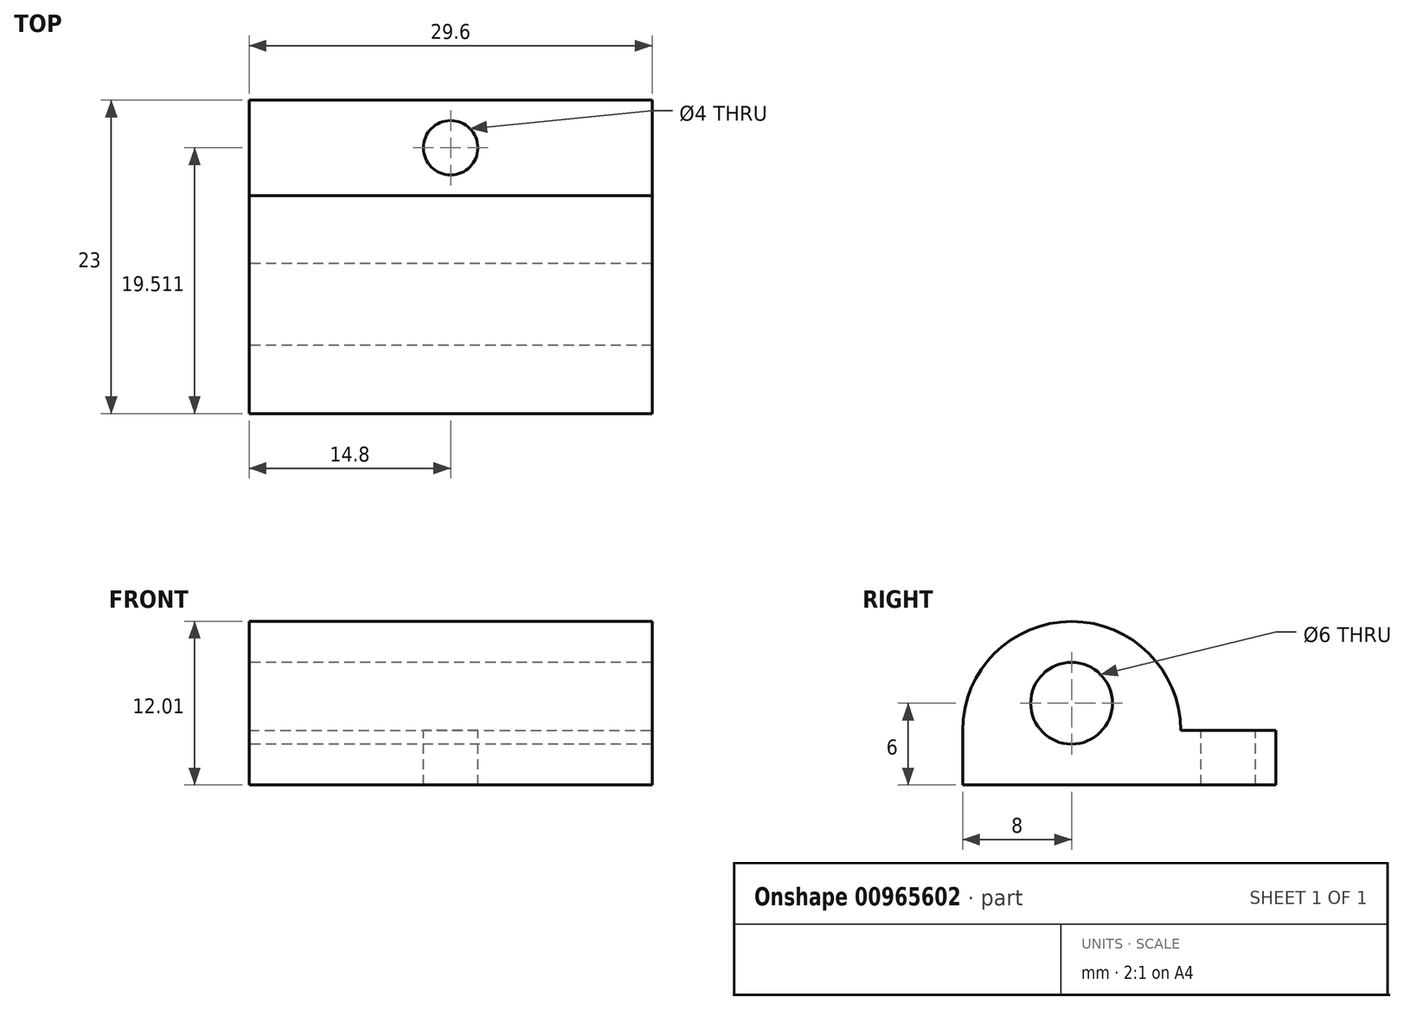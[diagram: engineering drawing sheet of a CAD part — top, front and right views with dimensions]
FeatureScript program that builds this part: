
annotation { "Feature Type Name" : "Feature", "Feature Type Description" : "" }
export const myFeature = defineFeature(function(context is Context, id is Id, definition is map)
    precondition{}
    {
        {
            var Q0;
            Q0=qCreatedBy(makeId("Top.planeOp"),FACE);
            var sketch = newSketch(context, id + "F0", { "sketchPlane" : qUnion([Q0])});
            skLineSegment(sketch, "E0.bottom", {"start": v(-14.8, 5) * mm, "end": v(14.8, 5) * mm});
            skLineSegment(sketch, "E0.top", {"start": v(-14.8, -5) * mm, "end": v(14.8, -5) * mm});
            skLineSegment(sketch, "E0.left", {"start": v(-14.8, 5) * mm, "end": v(-14.8, -5) * mm});
            skLineSegment(sketch, "E0.right", {"start": v(14.8, 5) * mm, "end": v(14.8, -5) * mm});
            skLineSegment(sketch, "E1.bottom", {"start": v(-14.8, 10) * mm, "end": v(14.8, 10) * mm});
            skLineSegment(sketch, "E1.top", {"start": v(-14.8, -10) * mm, "end": v(14.8, -10) * mm});
            skLineSegment(sketch, "E1.left", {"start": v(-14.8, 10) * mm, "end": v(-14.8, -10) * mm});
            skLineSegment(sketch, "E1.right", {"start": v(14.8, 10) * mm, "end": v(14.8, -10) * mm});
            skSolve(sketch);
        }
        {
            var Q0;
            {var subQ5=sQuery(id+"F0.wireOp",EDGE,"E1.bottom");Q0=makeQuery(id+"F0.imprint","IMPRINT",FACE,{"disambiguationData":[TD([[makeQuery(id+"F0.imprint","IMPRINT",EDGE,{"derivedFrom":subQ5}),-1.0]])]});}
            var Q1;
            {var subQ0=sQuery(id+"F0.wireOp",EDGE,"E1.left");var subQ1=sQuery(id+"F0.wireOp",EDGE,"E0.bottom");var subQ2=makeQuery(id+"F0.imprint","INTERSECT",VERTEX,{"derivedFrom":[subQ1,subQ0]});Q1=makeQuery(id+"F0.imprint","IMPRINT",FACE,{"disambiguationData":[TD([[makeQuery(id+"F0.imprint","IMPRINT",EDGE,{"disambiguationData":[TD([[subQ2,-1.0]])],"derivedFrom":subQ1}),-1.0]])]});}
            var Q2;
            {var subQ5=sQuery(id+"F0.wireOp",EDGE,"E1.top");Q2=makeQuery(id+"F0.imprint","IMPRINT",FACE,{"disambiguationData":[TD([[makeQuery(id+"F0.imprint","IMPRINT",EDGE,{"derivedFrom":subQ5}),1.0]])]});}
            var Q3;
            {var subQ0=sQuery(id+"F0.wireOp",EDGE,"E0.left");Q3=makeQuery(id+"F0.imprint","IMPRINT",FACE,{"disambiguationData":[TD([[makeQuery(id+"F0.imprint","IMPRINT",EDGE,{"derivedFrom":subQ0}),1.0]])]});}
            var Q4;
            {var subQ0=sQuery(id+"F0.wireOp",EDGE,"E0.right");Q4=makeQuery(id+"F0.imprint","IMPRINT",FACE,{"disambiguationData":[TD([[makeQuery(id+"F0.imprint","IMPRINT",EDGE,{"derivedFrom":subQ0}),-1.0]])]});}
            extrude(context, id + "F1", {"entities" : qUnion([Q0, Q1, Q2, Q3, Q4]), "depth" : 4 * mm, "offsetDistance" : 25 * mm});
        }
        {
            var Q0;
            Q0=makeQuery(id+"F1.opExtrude","SWEPT_FACE",FACE,{"disambiguationData":[OSD([sQuery(id+"F0.wireOp",EDGE,"E1.left")])]});
            var sketch = newSketch(context, id + "F2", { "sketchPlane" : qUnion([Q0])});
            skArc(sketch, "E2", {"start": v(10, 4) * mm, "mid": v(2, 12) * mm, "end": v(-6.01, 4) * mm});
            skSolve(sketch);
        }
        {
            var Q0;
            {var subQ0=sQuery(id+"F2.wireOp",EDGE,"E2");Q0=makeQuery(id+"F2.imprint","IMPRINT",FACE,{"disambiguationData":[TD([[makeQuery(id+"F2.imprint","IMPRINT",EDGE,{"derivedFrom":subQ0}),1.0]])]});}
            extrude(context, id + "F3", {"entities" : qUnion([Q0]), "operationType" : NewBodyOperationType.ADD, "depth" : -29.6 * mm, "offsetDistance" : 25 * mm});
        }
        {
            var Q0;
            {var subQ0=sQuery(id+"F0.wireOp",EDGE,"E1.left");Q0=makeQuery(id+"F3.boolean.opBoolean","MERGE",FACE,{"derivedFrom":[makeQuery(id+"F1.opExtrude","SWEPT_FACE",FACE,{"disambiguationData":[OSD([subQ0])]}),makeQuery(id+"F3.opExtrude","CAP_FACE",FACE,{"disambiguationData":[OSD([subQ0,sQuery(id+"F2.wireOp",EDGE,"E2")])],"isStart":true})]});}
            var sketch = newSketch(context, id + "F4", { "sketchPlane" : qUnion([Q0])});
            skCircle(sketch, "E3", {"center": v(2, 6) * mm, "radius": 3 * mm});
            skSolve(sketch);
        }
        {
            var Q0;
            Q0=makeQuery(id+"F4.imprint","IMPRINT",FACE,{"disambiguationData":[TD([[makeQuery(id+"F4.imprint","IMPRINT",EDGE,{"derivedFrom":sQuery(id+"F4.wireOp",EDGE,"E3")}),1.0]])]});
            extrude(context, id + "F5", {"entities" : qUnion([Q0]), "operationType" : NewBodyOperationType.REMOVE, "oppositeDirection" : true, "depth" : 33 * mm, "offsetDistance" : 25 * mm});
        }
        {
            var Q0;
            Q0=makeQuery(id+"F1.opExtrude","SWEPT_FACE",FACE,{"disambiguationData":[OSD([sQuery(id+"F0.wireOp",EDGE,"E1.bottom")])]});
            var sketch = newSketch(context, id + "F6", { "sketchPlane" : qUnion([Q0])});
            skLineSegment(sketch, "E4.bottom", {"start": v(-14.8, 4) * mm, "end": v(14.8, 4) * mm});
            skLineSegment(sketch, "E4.top", {"start": v(-14.8, 0) * mm, "end": v(14.8, 0) * mm});
            skLineSegment(sketch, "E4.left", {"start": v(-14.8, 4) * mm, "end": v(-14.8, 0) * mm});
            skLineSegment(sketch, "E4.right", {"start": v(14.8, 4) * mm, "end": v(14.8, 0) * mm});
            skSolve(sketch);
        }
        {
            var Q0;
            Q0=makeQuery(id+"F6.imprint","IMPRINT",FACE,{"disambiguationData":[TD([[makeQuery(id+"F6.imprint","IMPRINT",EDGE,{"derivedFrom":sQuery(id+"F6.wireOp",EDGE,"E4.bottom")}),1.0]])]});
            extrude(context, id + "F7", {"entities" : qUnion([Q0]), "operationType" : NewBodyOperationType.ADD, "depth" : 3 * mm, "offsetDistance" : 25 * mm});
        }
        {
            var Q0;
            Q0=makeQuery(id+"F7.boolean.opBoolean","MERGE",FACE,{"derivedFrom":[makeQuery(id+"F1.opExtrude","CAP_FACE",FACE,{"disambiguationData":[OSD([sQuery(id+"F0.wireOp",EDGE,"E1.bottom"),sQuery(id+"F0.wireOp",EDGE,"E1.top"),sQuery(id+"F0.wireOp",EDGE,"E1.left"),sQuery(id+"F0.wireOp",EDGE,"E1.right")])],"isStart":false}),makeQuery(id+"F7.opExtrude","SWEPT_FACE",FACE,{"disambiguationData":[OSD([sQuery(id+"F6.wireOp",EDGE,"E4.bottom")])]})]});
            var sketch = newSketch(context, id + "F8", { "sketchPlane" : qUnion([Q0])});
            skCircle(sketch, "E5", {"center": v(0, 9.51) * mm, "radius": 2 * mm});
            skSolve(sketch);
        }
        {
            var Q0;
            Q0=makeQuery(id+"F8.imprint","IMPRINT",FACE,{"disambiguationData":[TD([[makeQuery(id+"F8.imprint","IMPRINT",EDGE,{"derivedFrom":sQuery(id+"F8.wireOp",EDGE,"E5")}),1.0]])]});
            extrude(context, id + "F9", {"entities" : qUnion([Q0]), "operationType" : NewBodyOperationType.REMOVE, "oppositeDirection" : true, "depth" : 25 * mm, "offsetDistance" : 25 * mm});
        }
    });
